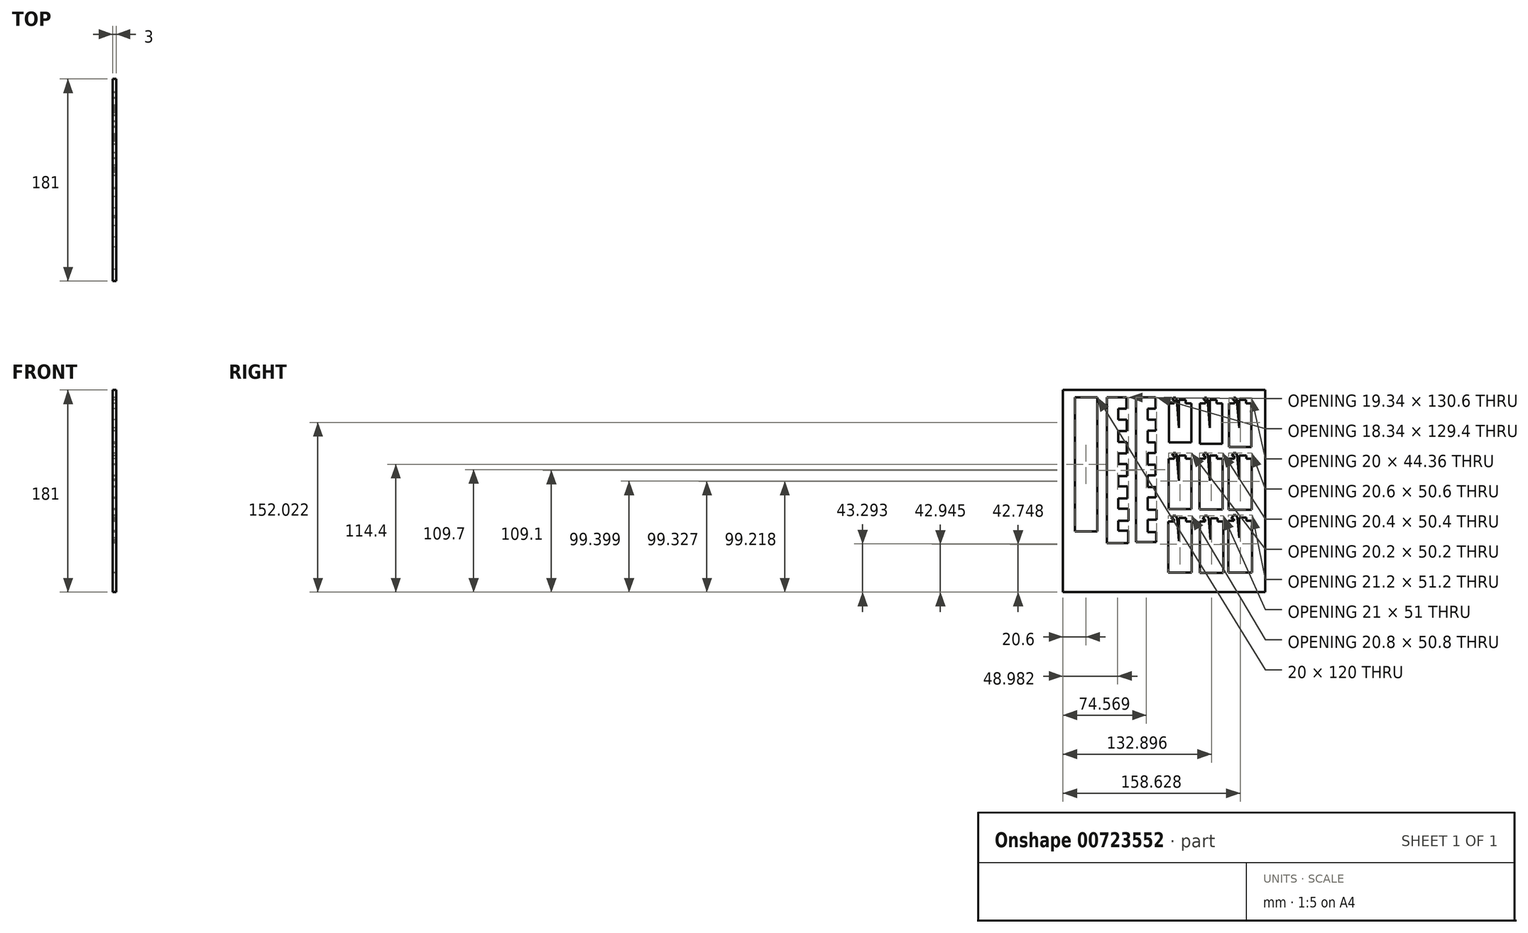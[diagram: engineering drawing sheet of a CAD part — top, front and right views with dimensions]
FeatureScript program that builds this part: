
annotation { "Feature Type Name" : "Feature", "Feature Type Description" : "" }
export const myFeature = defineFeature(function(context is Context, id is Id, definition is map)
    precondition{}
    {
        {
            var Q0;
            Q0=qCreatedBy(makeId("Right.planeOp"),FACE);
            var sketch = newSketch(context, id + "F0", { "sketchPlane" : qUnion([Q0])});
            skLineSegment(sketch, "E0.bottom", {"start": v(-90.5, 90.5) * mm, "end": v(90.5, 90.5) * mm});
            skLineSegment(sketch, "E0.top", {"start": v(-90.5, -90.5) * mm, "end": v(90.5, -90.5) * mm});
            skLineSegment(sketch, "E0.left", {"start": v(-90.5, 90.5) * mm, "end": v(-90.5, -90.5) * mm});
            skLineSegment(sketch, "E0.right", {"start": v(90.5, 90.5) * mm, "end": v(90.5, -90.5) * mm});
            skLineSegment(sketch, "E1.bottom", {"start": v(-74.9, 25.4) * mm, "end": v(-64.9, 25.4) * mm});
            skLineSegment(sketch, "E1.top", {"start": v(-74.9, 22.4) * mm, "end": v(-64.9, 22.4) * mm});
            skLineSegment(sketch, "E1.left", {"start": v(-74.9, 25.4) * mm, "end": v(-74.9, 22.4) * mm});
            skLineSegment(sketch, "E1.right", {"start": v(-64.9, 25.4) * mm, "end": v(-64.9, 22.4) * mm});
            skLineSegment(sketch, "E2.bottom", {"start": v(-79.9, 83.9) * mm, "end": v(-59.9, 83.9) * mm});
            skLineSegment(sketch, "E2.top", {"start": v(-79.9, -36.1) * mm, "end": v(-59.9, -36.1) * mm});
            skLineSegment(sketch, "E2.left", {"start": v(-79.9, 83.9) * mm, "end": v(-79.9, -36.1) * mm});
            skLineSegment(sketch, "E2.right", {"start": v(-59.9, 83.9) * mm, "end": v(-59.9, -36.1) * mm});
            skLineSegment(sketch, "E3.0", {"start": v(-75, 35.5) * mm, "end": v(-75, 32.3) * mm});
            skLineSegment(sketch, "E3.1", {"start": v(-75, 35.5) * mm, "end": v(-64.8, 35.5) * mm});
            skLineSegment(sketch, "E3.2", {"start": v(-64.8, 35.5) * mm, "end": v(-64.8, 32.3) * mm});
            skLineSegment(sketch, "E3.3", {"start": v(-75, 32.3) * mm, "end": v(-64.8, 32.3) * mm});
            skLineSegment(sketch, "E4.0", {"start": v(-75.1, 45.6) * mm, "end": v(-64.7, 45.6) * mm});
            skLineSegment(sketch, "E4.1", {"start": v(-75.1, 45.6) * mm, "end": v(-75.1, 42.2) * mm});
            skLineSegment(sketch, "E4.2", {"start": v(-75.1, 42.2) * mm, "end": v(-64.7, 42.2) * mm});
            skLineSegment(sketch, "E4.3", {"start": v(-64.7, 45.6) * mm, "end": v(-64.7, 42.2) * mm});
            skLineSegment(sketch, "E5.0", {"start": v(-75.2, 52.1) * mm, "end": v(-64.6, 52.1) * mm});
            skLineSegment(sketch, "E5.1", {"start": v(-75.2, 55.7) * mm, "end": v(-75.2, 52.1) * mm});
            skLineSegment(sketch, "E5.2", {"start": v(-75.2, 55.7) * mm, "end": v(-64.6, 55.7) * mm});
            skLineSegment(sketch, "E5.3", {"start": v(-64.6, 55.7) * mm, "end": v(-64.6, 52.1) * mm});
            skLineSegment(sketch, "E6.0", {"start": v(-75.3, 62) * mm, "end": v(-64.5, 62) * mm});
            skLineSegment(sketch, "E6.1", {"start": v(-75.3, 65.8) * mm, "end": v(-75.3, 62) * mm});
            skLineSegment(sketch, "E6.2", {"start": v(-75.3, 65.8) * mm, "end": v(-64.5, 65.8) * mm});
            skLineSegment(sketch, "E6.3", {"start": v(-64.5, 65.8) * mm, "end": v(-64.5, 62) * mm});
            skLineSegment(sketch, "E7.0", {"start": v(-75.4, 71.9) * mm, "end": v(-64.4, 71.9) * mm});
            skLineSegment(sketch, "E7.1", {"start": v(-75.4, 75.9) * mm, "end": v(-75.4, 71.9) * mm});
            skLineSegment(sketch, "E7.2", {"start": v(-75.4, 75.9) * mm, "end": v(-64.4, 75.9) * mm});
            skLineSegment(sketch, "E7.3", {"start": v(-64.4, 75.9) * mm, "end": v(-64.4, 71.9) * mm});
            skLineSegment(sketch, "E8.0", {"start": v(-74.8, 15.3) * mm, "end": v(-74.8, 12.5) * mm});
            skLineSegment(sketch, "E8.1", {"start": v(-74.8, 15.3) * mm, "end": v(-65, 15.3) * mm});
            skLineSegment(sketch, "E8.2", {"start": v(-65, 15.3) * mm, "end": v(-65, 12.5) * mm});
            skLineSegment(sketch, "E8.3", {"start": v(-74.8, 12.5) * mm, "end": v(-65, 12.5) * mm});
            skLineSegment(sketch, "E9.0", {"start": v(-74.7, 5.2) * mm, "end": v(-74.7, 2.6) * mm});
            skLineSegment(sketch, "E9.1", {"start": v(-74.7, 5.2) * mm, "end": v(-65.1, 5.2) * mm});
            skLineSegment(sketch, "E9.2", {"start": v(-65.1, 5.2) * mm, "end": v(-65.1, 2.6) * mm});
            skLineSegment(sketch, "E9.3", {"start": v(-74.7, 2.6) * mm, "end": v(-65.1, 2.6) * mm});
            skLineSegment(sketch, "E10.0", {"start": v(-65.2, -4.9) * mm, "end": v(-65.2, -7.3) * mm});
            skLineSegment(sketch, "E10.1", {"start": v(-74.6, -4.9) * mm, "end": v(-65.2, -4.9) * mm});
            skLineSegment(sketch, "E10.2", {"start": v(-74.6, -4.9) * mm, "end": v(-74.6, -7.3) * mm});
            skLineSegment(sketch, "E10.3", {"start": v(-74.6, -7.3) * mm, "end": v(-65.2, -7.3) * mm});
            skLineSegment(sketch, "E11.0", {"start": v(-74.5, -15) * mm, "end": v(-65.3, -15) * mm});
            skLineSegment(sketch, "E11.1", {"start": v(-74.5, -15) * mm, "end": v(-74.5, -17.2) * mm});
            skLineSegment(sketch, "E11.2", {"start": v(-74.5, -17.2) * mm, "end": v(-65.3, -17.2) * mm});
            skLineSegment(sketch, "E11.3", {"start": v(-65.3, -15) * mm, "end": v(-65.3, -17.2) * mm});
            skLineSegment(sketch, "E12.0", {"start": v(-74.4, -25.1) * mm, "end": v(-74.4, -27.1) * mm});
            skLineSegment(sketch, "E12.1", {"start": v(-74.4, -25.1) * mm, "end": v(-65.4, -25.1) * mm});
            skLineSegment(sketch, "E12.2", {"start": v(-65.4, -25.1) * mm, "end": v(-65.4, -27.1) * mm});
            skLineSegment(sketch, "E12.3", {"start": v(-74.4, -27.1) * mm, "end": v(-65.4, -27.1) * mm});
            skLineSegment(sketch, "E13.left", {"start": v(-51.19, 83.9) * mm, "end": v(-51.19, -46.7) * mm});
            skLineSegment(sketch, "E13.right", {"start": v(-40.86, 73.9) * mm, "end": v(-40.86, 64) * mm});
            skLineSegment(sketch, "E14.top", {"start": v(-40.86, 73.9) * mm, "end": v(-33.86, 73.9) * mm});
            skLineSegment(sketch, "E14.right", {"start": v(-33.86, 83.9) * mm, "end": v(-33.86, 73.9) * mm});
            skLineSegment(sketch, "E15.trimOffspring", {"start": v(-40.86, 53.8) * mm, "end": v(-40.86, 44.1) * mm});
            skLineSegment(sketch, "E16.trimOffspring", {"start": v(-40.86, 33.7) * mm, "end": v(-40.86, 24.2) * mm});
            skLineSegment(sketch, "E17.trimOffspring", {"start": v(-40.86, 13.6) * mm, "end": v(-40.86, 4.3) * mm});
            skLineSegment(sketch, "E18.trimOffspring", {"start": v(-40.86, -6.5) * mm, "end": v(-40.86, -15.6) * mm});
            skLineSegment(sketch, "E19.trimOffspring", {"start": v(-40.86, -26.6) * mm, "end": v(-40.86, -35.5) * mm});
            skLineSegment(sketch, "E20.0", {"start": v(-40.86, 53.8) * mm, "end": v(-33.4, 53.8) * mm});
            skLineSegment(sketch, "E20.1", {"start": v(-33.4, 64) * mm, "end": v(-33.4, 53.8) * mm});
            skLineSegment(sketch, "E20.2", {"start": v(-40.86, 64) * mm, "end": v(-33.4, 64) * mm});
            skLineSegment(sketch, "E21.0", {"start": v(-40.86, 33.7) * mm, "end": v(-33.3, 33.7) * mm});
            skLineSegment(sketch, "E21.1", {"start": v(-33.3, 44.1) * mm, "end": v(-33.3, 33.7) * mm});
            skLineSegment(sketch, "E21.2", {"start": v(-40.86, 44.1) * mm, "end": v(-33.3, 44.1) * mm});
            skLineSegment(sketch, "E22.0", {"start": v(-40.86, 13.6) * mm, "end": v(-33.2, 13.6) * mm});
            skLineSegment(sketch, "E22.1", {"start": v(-33.2, 24.2) * mm, "end": v(-33.2, 13.6) * mm});
            skLineSegment(sketch, "E22.2", {"start": v(-40.86, 24.2) * mm, "end": v(-33.2, 24.2) * mm});
            skLineSegment(sketch, "E23.0", {"start": v(-40.86, -6.5) * mm, "end": v(-32.69, -6.5) * mm});
            skLineSegment(sketch, "E23.1", {"start": v(-32.69, 4.3) * mm, "end": v(-32.69, -6.5) * mm});
            skLineSegment(sketch, "E23.2", {"start": v(-40.86, 4.3) * mm, "end": v(-32.69, 4.3) * mm});
            skLineSegment(sketch, "E24.0", {"start": v(-40.86, -26.6) * mm, "end": v(-31.85, -26.6) * mm});
            skLineSegment(sketch, "E24.1", {"start": v(-31.85, -15.6) * mm, "end": v(-31.85, -26.6) * mm});
            skLineSegment(sketch, "E24.2", {"start": v(-40.86, -15.6) * mm, "end": v(-31.85, -15.6) * mm});
            skLineSegment(sketch, "E25.1", {"start": v(-32, -35.5) * mm, "end": v(-32, -46.7) * mm});
            skLineSegment(sketch, "E25.2", {"start": v(-40.86, -35.5) * mm, "end": v(-32, -35.5) * mm});
            skLineSegment(sketch, "E26.top", {"start": v(-14.77, 73.9) * mm, "end": v(-7.77, 73.9) * mm});
            skLineSegment(sketch, "E26.right", {"start": v(-7.77, 83.9) * mm, "end": v(-7.77, 73.9) * mm});
            skLineSegment(sketch, "E27.0", {"start": v(-14.77, 54) * mm, "end": v(-7.51, 54) * mm});
            skLineSegment(sketch, "E27.1", {"start": v(-7.51, 63.8) * mm, "end": v(-7.51, 54) * mm});
            skLineSegment(sketch, "E27.2", {"start": v(-14.77, 63.8) * mm, "end": v(-7.51, 63.8) * mm});
            skLineSegment(sketch, "E28.0", {"start": v(-14.77, 34.1) * mm, "end": v(-7.61, 34.1) * mm});
            skLineSegment(sketch, "E28.1", {"start": v(-7.61, 43.7) * mm, "end": v(-7.61, 34.1) * mm});
            skLineSegment(sketch, "E28.2", {"start": v(-14.77, 43.7) * mm, "end": v(-7.61, 43.7) * mm});
            skLineSegment(sketch, "E29.0", {"start": v(-14.77, 14.2) * mm, "end": v(-7.71, 14.2) * mm});
            skLineSegment(sketch, "E29.1", {"start": v(-7.71, 23.6) * mm, "end": v(-7.71, 14.2) * mm});
            skLineSegment(sketch, "E29.2", {"start": v(-14.77, 23.6) * mm, "end": v(-7.71, 23.6) * mm});
            skLineSegment(sketch, "E30.0", {"start": v(-14.77, -5.7) * mm, "end": v(-7.4, -5.7) * mm});
            skLineSegment(sketch, "E30.1", {"start": v(-7.4, 3.5) * mm, "end": v(-7.4, -5.7) * mm});
            skLineSegment(sketch, "E30.2", {"start": v(-14.77, 3.5) * mm, "end": v(-7.4, 3.5) * mm});
            skLineSegment(sketch, "E31.0", {"start": v(-14.77, -25.6) * mm, "end": v(-6.76, -25.6) * mm});
            skLineSegment(sketch, "E31.1", {"start": v(-6.76, -16.6) * mm, "end": v(-6.76, -25.6) * mm});
            skLineSegment(sketch, "E31.2", {"start": v(-14.77, -16.6) * mm, "end": v(-6.76, -16.6) * mm});
            skLineSegment(sketch, "E32.1", {"start": v(-7.11, -36.7) * mm, "end": v(-7.11, -45.5) * mm});
            skLineSegment(sketch, "E32.2", {"start": v(-14.77, -36.7) * mm, "end": v(-7.11, -36.7) * mm});
            skLineSegment(sketch, "E33", {"start": v(-51.19, -46.7) * mm, "end": v(-32, -46.7) * mm});
            skLineSegment(sketch, "E34", {"start": v(-51.19, 83.9) * mm, "end": v(-33.86, 83.9) * mm});
            skLineSegment(sketch, "E35", {"start": v(-25.1, 83.9) * mm, "end": v(-7.77, 83.9) * mm});
            skLineSegment(sketch, "E36", {"start": v(-25.1, -45.5) * mm, "end": v(-7.11, -45.5) * mm});
            skLineSegment(sketch, "E37", {"start": v(-14.77, 54) * mm, "end": v(-14.77, 43.7) * mm});
            skLineSegment(sketch, "E38", {"start": v(-14.77, 34.1) * mm, "end": v(-14.77, 23.6) * mm});
            skLineSegment(sketch, "E39", {"start": v(-14.77, 14.2) * mm, "end": v(-14.77, 3.5) * mm});
            skLineSegment(sketch, "E40", {"start": v(-14.77, -5.7) * mm, "end": v(-14.77, -16.6) * mm});
            skLineSegment(sketch, "E41", {"start": v(-14.77, -25.6) * mm, "end": v(-14.77, -36.7) * mm});
            skLineSegment(sketch, "E42", {"start": v(-25.1, 83.9) * mm, "end": v(-25.1, -45.5) * mm});
            skLineSegment(sketch, "E43", {"start": v(-14.77, 73.9) * mm, "end": v(-14.77, 63.8) * mm});
            skLineSegment(sketch, "E44.bottom", {"start": v(4.26, 78.7) * mm, "end": v(9.26, 78.7) * mm});
            skLineSegment(sketch, "E44.top", {"start": v(4.26, 43.7) * mm, "end": v(24.26, 43.7) * mm});
            skLineSegment(sketch, "E44.left", {"start": v(4.26, 78.7) * mm, "end": v(4.26, 43.7) * mm});
            skLineSegment(sketch, "E44.right", {"start": v(24.26, 78.7) * mm, "end": v(24.26, 43.7) * mm});
            skLineSegment(sketch, "E45.top", {"start": v(13.26, 81.7) * mm, "end": v(19.26, 81.7) * mm});
            skLineSegment(sketch, "E45.right", {"start": v(19.26, 78.7) * mm, "end": v(19.26, 81.7) * mm});
            skLineSegment(sketch, "E46", {"start": v(13.26, 56.7) * mm, "end": v(11.26, 81.7) * mm});
            skLineSegment(sketch, "E47", {"start": v(11.26, 81.7) * mm, "end": v(10.26, 83.7) * mm});
            skLineSegment(sketch, "E48", {"start": v(10.26, 83.7) * mm, "end": v(8.26, 83.7) * mm});
            skLineSegment(sketch, "E49", {"start": v(8.26, 83.7) * mm, "end": v(7.26, 81.7) * mm});
            skLineSegment(sketch, "E50", {"start": v(7.26, 81.7) * mm, "end": v(9.26, 81.7) * mm});
            skLineSegment(sketch, "E51.trimOffspring", {"start": v(19.26, 78.7) * mm, "end": v(24.26, 78.7) * mm});
            skLineSegment(sketch, "E52", {"start": v(13.26, 81.7) * mm, "end": v(13.26, 56.7) * mm});
            skLineSegment(sketch, "E53.bottom", {"start": v(32.03, 78.7) * mm, "end": v(37.03, 78.7) * mm});
            skLineSegment(sketch, "E53.top", {"start": v(32.03, 42.25) * mm, "end": v(52.03, 42.25) * mm});
            skLineSegment(sketch, "E53.left", {"start": v(32.03, 78.7) * mm, "end": v(32.03, 42.25) * mm});
            skLineSegment(sketch, "E53.right", {"start": v(52.03, 78.7) * mm, "end": v(52.03, 42.25) * mm});
            skLineSegment(sketch, "E54.top", {"start": v(41.03, 81.7) * mm, "end": v(47.03, 81.7) * mm});
            skLineSegment(sketch, "E54.right", {"start": v(47.03, 78.7) * mm, "end": v(47.03, 81.7) * mm});
            skLineSegment(sketch, "E55", {"start": v(41.03, 56.7) * mm, "end": v(39.03, 81.7) * mm});
            skLineSegment(sketch, "E56", {"start": v(39.03, 81.7) * mm, "end": v(38.03, 83.7) * mm});
            skLineSegment(sketch, "E57", {"start": v(38.03, 83.7) * mm, "end": v(36.03, 83.7) * mm});
            skLineSegment(sketch, "E58", {"start": v(36.03, 83.7) * mm, "end": v(35.03, 81.7) * mm});
            skLineSegment(sketch, "E59", {"start": v(35.03, 81.7) * mm, "end": v(37.03, 81.7) * mm});
            skLineSegment(sketch, "E60.trimOffspring", {"start": v(47.03, 78.7) * mm, "end": v(52.03, 78.7) * mm});
            skLineSegment(sketch, "E61", {"start": v(41.03, 81.7) * mm, "end": v(41.03, 56.7) * mm});
            skLineSegment(sketch, "E62.bottom", {"start": v(58.13, 78.7) * mm, "end": v(63.13, 78.7) * mm});
            skLineSegment(sketch, "E62.top", {"start": v(58.13, 39.34) * mm, "end": v(78.13, 39.34) * mm});
            skLineSegment(sketch, "E62.left", {"start": v(58.13, 78.7) * mm, "end": v(58.13, 39.34) * mm});
            skLineSegment(sketch, "E62.right", {"start": v(78.13, 78.7) * mm, "end": v(78.13, 39.34) * mm});
            skLineSegment(sketch, "E63.top", {"start": v(67.13, 81.7) * mm, "end": v(73.13, 81.7) * mm});
            skLineSegment(sketch, "E63.right", {"start": v(73.13, 78.7) * mm, "end": v(73.13, 81.7) * mm});
            skLineSegment(sketch, "E64", {"start": v(67.13, 56.7) * mm, "end": v(65.13, 81.7) * mm});
            skLineSegment(sketch, "E65", {"start": v(65.13, 81.7) * mm, "end": v(64.13, 83.7) * mm});
            skLineSegment(sketch, "E66", {"start": v(64.13, 83.7) * mm, "end": v(62.13, 83.7) * mm});
            skLineSegment(sketch, "E67", {"start": v(62.13, 83.7) * mm, "end": v(61.13, 81.7) * mm});
            skLineSegment(sketch, "E68", {"start": v(61.13, 81.7) * mm, "end": v(63.13, 81.7) * mm});
            skLineSegment(sketch, "E69.trimOffspring", {"start": v(73.13, 78.7) * mm, "end": v(78.13, 78.7) * mm});
            skLineSegment(sketch, "E70", {"start": v(67.13, 81.7) * mm, "end": v(67.13, 56.7) * mm});
            skLineSegment(sketch, "E71", {"start": v(63.13, 51.7) * mm, "end": v(63.13, 78.7) * mm});
            skLineSegment(sketch, "E72", {"start": v(37.03, 54.7) * mm, "end": v(37.03, 78.7) * mm});
            skLineSegment(sketch, "E73", {"start": v(9.26, 56.7) * mm, "end": v(9.26, 78.7) * mm});
            skLineSegment(sketch, "E74", {"start": v(9.26, 81.7) * mm, "end": v(9.26, 78.7) * mm});
            skLineSegment(sketch, "E75", {"start": v(37.03, 81.7) * mm, "end": v(37.03, 78.7) * mm});
            skLineSegment(sketch, "E76", {"start": v(63.13, 81.7) * mm, "end": v(63.13, 78.7) * mm});
            skLineSegment(sketch, "E77.0", {"start": v(19.36, 29) * mm, "end": v(19.36, 32) * mm});
            skLineSegment(sketch, "E77.1", {"start": v(13.16, 32) * mm, "end": v(19.36, 32) * mm});
            skLineSegment(sketch, "E77.2", {"start": v(13.16, 32) * mm, "end": v(13.16, 9.4) * mm});
            skLineSegment(sketch, "E77.3", {"start": v(4.16, 29) * mm, "end": v(9.16, 29) * mm});
            skLineSegment(sketch, "E77.7", {"start": v(9.16, 31.8) * mm, "end": v(9.16, 29) * mm});
            skLineSegment(sketch, "E77.8", {"start": v(7.1, 31.8) * mm, "end": v(9.16, 31.8) * mm});
            skLineSegment(sketch, "E77.9", {"start": v(8.2, 34) * mm, "end": v(7.1, 31.8) * mm});
            skLineSegment(sketch, "E77.10", {"start": v(19.36, 29) * mm, "end": v(24.36, 29) * mm});
            skLineSegment(sketch, "E77.11", {"start": v(10.33, 34) * mm, "end": v(8.2, 34) * mm});
            skLineSegment(sketch, "E77.12", {"start": v(11.36, 31.93) * mm, "end": v(10.33, 34) * mm});
            skLineSegment(sketch, "E77.13", {"start": v(13.16, 9.4) * mm, "end": v(11.36, 31.93) * mm});
            skLineSegment(sketch, "E78.2", {"start": v(39.22, 31.88) * mm, "end": v(38.15, 34.03) * mm});
            skLineSegment(sketch, "E78.5", {"start": v(47.23, 29.03) * mm, "end": v(52.23, 29.03) * mm});
            skLineSegment(sketch, "E78.6", {"start": v(47.23, 29.03) * mm, "end": v(47.23, 32.03) * mm});
            skLineSegment(sketch, "E78.8", {"start": v(31.83, 29.03) * mm, "end": v(36.83, 29.03) * mm});
            skLineSegment(sketch, "E78.9", {"start": v(36.83, 31.63) * mm, "end": v(36.83, 29.03) * mm});
            skLineSegment(sketch, "E78.10", {"start": v(41.03, 32.03) * mm, "end": v(47.23, 32.03) * mm});
            skLineSegment(sketch, "E78.11", {"start": v(34.7, 31.63) * mm, "end": v(36.83, 31.63) * mm});
            skLineSegment(sketch, "E78.12", {"start": v(35.9, 34.03) * mm, "end": v(34.7, 31.63) * mm});
            skLineSegment(sketch, "E78.13", {"start": v(38.15, 34.03) * mm, "end": v(35.9, 34.03) * mm});
            skLineSegment(sketch, "E79.0", {"start": v(73.43, 29.02) * mm, "end": v(73.43, 32.02) * mm});
            skLineSegment(sketch, "E79.1", {"start": v(67.13, 32.02) * mm, "end": v(73.43, 32.02) * mm});
            skLineSegment(sketch, "E79.3", {"start": v(57.83, 29.02) * mm, "end": v(62.83, 29.02) * mm});
            skLineSegment(sketch, "E79.7", {"start": v(62.83, 31.42) * mm, "end": v(62.83, 29.02) * mm});
            skLineSegment(sketch, "E79.8", {"start": v(60.64, 31.42) * mm, "end": v(62.83, 31.42) * mm});
            skLineSegment(sketch, "E79.9", {"start": v(61.94, 34.02) * mm, "end": v(60.64, 31.42) * mm});
            skLineSegment(sketch, "E79.10", {"start": v(73.43, 29.02) * mm, "end": v(78.43, 29.02) * mm});
            skLineSegment(sketch, "E79.11", {"start": v(64.31, 34.02) * mm, "end": v(61.94, 34.02) * mm});
            skLineSegment(sketch, "E79.12", {"start": v(65.42, 31.8) * mm, "end": v(64.31, 34.02) * mm});
            skLineSegment(sketch, "E80.3", {"start": v(10.51, -22.16) * mm, "end": v(8.02, -22.16) * mm});
            skLineSegment(sketch, "E80.4", {"start": v(8.02, -22.16) * mm, "end": v(6.62, -24.96) * mm});
            skLineSegment(sketch, "E80.5", {"start": v(6.62, -24.96) * mm, "end": v(8.86, -24.96) * mm});
            skLineSegment(sketch, "E80.6", {"start": v(8.86, -24.96) * mm, "end": v(8.86, -27.16) * mm});
            skLineSegment(sketch, "E80.7", {"start": v(11.66, -24.45) * mm, "end": v(10.51, -22.16) * mm});
            skLineSegment(sketch, "E80.10", {"start": v(3.86, -27.16) * mm, "end": v(8.86, -27.16) * mm});
            skLineSegment(sketch, "E80.11", {"start": v(13.26, -24.16) * mm, "end": v(19.66, -24.16) * mm});
            skLineSegment(sketch, "E80.12", {"start": v(19.66, -27.16) * mm, "end": v(19.66, -24.16) * mm});
            skLineSegment(sketch, "E80.13", {"start": v(19.66, -27.16) * mm, "end": v(24.66, -27.16) * mm});
            skLineSegment(sketch, "E81.0", {"start": v(31.9, -27.25) * mm, "end": v(36.9, -27.25) * mm});
            skLineSegment(sketch, "E81.1", {"start": v(36.9, -25.25) * mm, "end": v(36.9, -27.25) * mm});
            skLineSegment(sketch, "E81.2", {"start": v(34.59, -25.25) * mm, "end": v(36.9, -25.25) * mm});
            skLineSegment(sketch, "E81.3", {"start": v(47.9, -27.25) * mm, "end": v(47.9, -24.25) * mm});
            skLineSegment(sketch, "E81.4", {"start": v(47.9, -27.25) * mm, "end": v(52.9, -27.25) * mm});
            skLineSegment(sketch, "E81.7", {"start": v(41.4, -24.25) * mm, "end": v(47.9, -24.25) * mm});
            skLineSegment(sketch, "E81.11", {"start": v(39.89, -24.61) * mm, "end": v(38.7, -22.25) * mm});
            skLineSegment(sketch, "E81.12", {"start": v(38.7, -22.25) * mm, "end": v(36.09, -22.25) * mm});
            skLineSegment(sketch, "E81.13", {"start": v(36.09, -22.25) * mm, "end": v(34.59, -25.25) * mm});
            skLineSegment(sketch, "E82.0", {"start": v(73.73, -26.6) * mm, "end": v(78.73, -26.6) * mm});
            skLineSegment(sketch, "E82.1", {"start": v(73.73, -26.6) * mm, "end": v(73.73, -23.6) * mm});
            skLineSegment(sketch, "E82.2", {"start": v(67.13, -23.6) * mm, "end": v(73.73, -23.6) * mm});
            skLineSegment(sketch, "E82.3", {"start": v(62.53, -24.8) * mm, "end": v(62.53, -26.6) * mm});
            skLineSegment(sketch, "E82.4", {"start": v(57.53, -26.6) * mm, "end": v(62.53, -26.6) * mm});
            skLineSegment(sketch, "E82.7", {"start": v(60.16, -24.8) * mm, "end": v(62.53, -24.8) * mm});
            skLineSegment(sketch, "E82.8", {"start": v(61.76, -21.6) * mm, "end": v(60.16, -24.8) * mm});
            skLineSegment(sketch, "E82.9", {"start": v(64.5, -21.6) * mm, "end": v(61.76, -21.6) * mm});
            skLineSegment(sketch, "E82.11", {"start": v(65.72, -24.04) * mm, "end": v(64.5, -21.6) * mm});
            skLineSegment(sketch, "E83", {"start": v(41.03, 9.34) * mm, "end": v(39.22, 31.88) * mm});
            skLineSegment(sketch, "E84", {"start": v(41.03, 32.03) * mm, "end": v(41.03, 9.34) * mm});
            skLineSegment(sketch, "E85", {"start": v(65.42, 31.8) * mm, "end": v(67.13, 10.48) * mm});
            skLineSegment(sketch, "E86", {"start": v(67.13, 32.02) * mm, "end": v(67.13, 10.48) * mm});
            skLineSegment(sketch, "E87", {"start": v(11.66, -24.45) * mm, "end": v(13.26, -44.54) * mm});
            skLineSegment(sketch, "E88", {"start": v(13.26, -24.16) * mm, "end": v(13.26, -44.54) * mm});
            skLineSegment(sketch, "E89", {"start": v(41.4, -24.25) * mm, "end": v(41.4, -43.48) * mm});
            skLineSegment(sketch, "E90", {"start": v(39.89, -24.61) * mm, "end": v(41.4, -43.48) * mm});
            skLineSegment(sketch, "E91", {"start": v(65.72, -24.04) * mm, "end": v(67.13, -41.68) * mm});
            skLineSegment(sketch, "E92", {"start": v(67.13, -23.6) * mm, "end": v(67.13, -41.68) * mm});
            skLineSegment(sketch, "E93", {"start": v(9.16, 29) * mm, "end": v(9.16, 1.99) * mm});
            skLineSegment(sketch, "E94", {"start": v(36.83, 29.03) * mm, "end": v(36.83, 2.02) * mm});
            skLineSegment(sketch, "E95", {"start": v(62.83, 29.02) * mm, "end": v(62.83, 1.9) * mm});
            skLineSegment(sketch, "E96", {"start": v(8.86, -27.16) * mm, "end": v(8.86, -54.27) * mm});
            skLineSegment(sketch, "E97", {"start": v(36.9, -27.25) * mm, "end": v(36.9, -54.47) * mm});
            skLineSegment(sketch, "E98", {"start": v(62.53, -26.6) * mm, "end": v(62.53, -53.78) * mm});
            skLineSegment(sketch, "E99.top", {"start": v(4.16, -16.2) * mm, "end": v(24.36, -16.2) * mm});
            skLineSegment(sketch, "E100.top", {"start": v(31.83, -16.37) * mm, "end": v(52.23, -16.37) * mm});
            skLineSegment(sketch, "E101.top", {"start": v(57.83, -16.58) * mm, "end": v(78.43, -16.58) * mm});
            skLineSegment(sketch, "E102.top", {"start": v(3.86, -72.96) * mm, "end": v(24.66, -72.96) * mm});
            skLineSegment(sketch, "E103.top", {"start": v(31.9, -73.25) * mm, "end": v(52.9, -73.25) * mm});
            skLineSegment(sketch, "E104.top", {"start": v(57.53, -72.8) * mm, "end": v(78.73, -72.8) * mm});
            skLineSegment(sketch, "E105", {"start": v(3.86, -27.16) * mm, "end": v(3.86, -72.96) * mm});
            skLineSegment(sketch, "E106", {"start": v(24.66, -27.16) * mm, "end": v(24.66, -72.96) * mm});
            skLineSegment(sketch, "E107", {"start": v(31.9, -27.25) * mm, "end": v(31.9, -73.25) * mm});
            skLineSegment(sketch, "E108", {"start": v(52.9, -27.25) * mm, "end": v(52.9, -73.25) * mm});
            skLineSegment(sketch, "E109", {"start": v(57.53, -26.6) * mm, "end": v(57.53, -72.8) * mm});
            skLineSegment(sketch, "E110", {"start": v(78.73, -26.6) * mm, "end": v(78.73, -72.8) * mm});
            skLineSegment(sketch, "E111", {"start": v(4.16, 29) * mm, "end": v(4.16, -16.2) * mm});
            skLineSegment(sketch, "E112", {"start": v(24.36, 29) * mm, "end": v(24.36, -16.2) * mm});
            skLineSegment(sketch, "E113", {"start": v(31.83, 29.03) * mm, "end": v(31.83, -16.37) * mm});
            skLineSegment(sketch, "E114", {"start": v(52.23, 29.03) * mm, "end": v(52.23, -16.37) * mm});
            skLineSegment(sketch, "E115", {"start": v(57.83, 29.02) * mm, "end": v(57.83, -16.58) * mm});
            skLineSegment(sketch, "E116", {"start": v(78.43, 29.02) * mm, "end": v(78.43, -16.58) * mm});
            skSolve(sketch);
        }
        {
            var Q0;
            Q0=makeQuery(id+"F0.imprint","IMPRINT",FACE,{"disambiguationData":[TD([[makeQuery(id+"F0.imprint","IMPRINT",EDGE,{"derivedFrom":sQuery(id+"F0.wireOp",EDGE,"E0.bottom")}),-1.0]])]});
            extrude(context, id + "F1", {"entities" : qUnion([Q0]), "depth" : 3 * mm, "offsetDistance" : 25 * mm});
        }
    });
